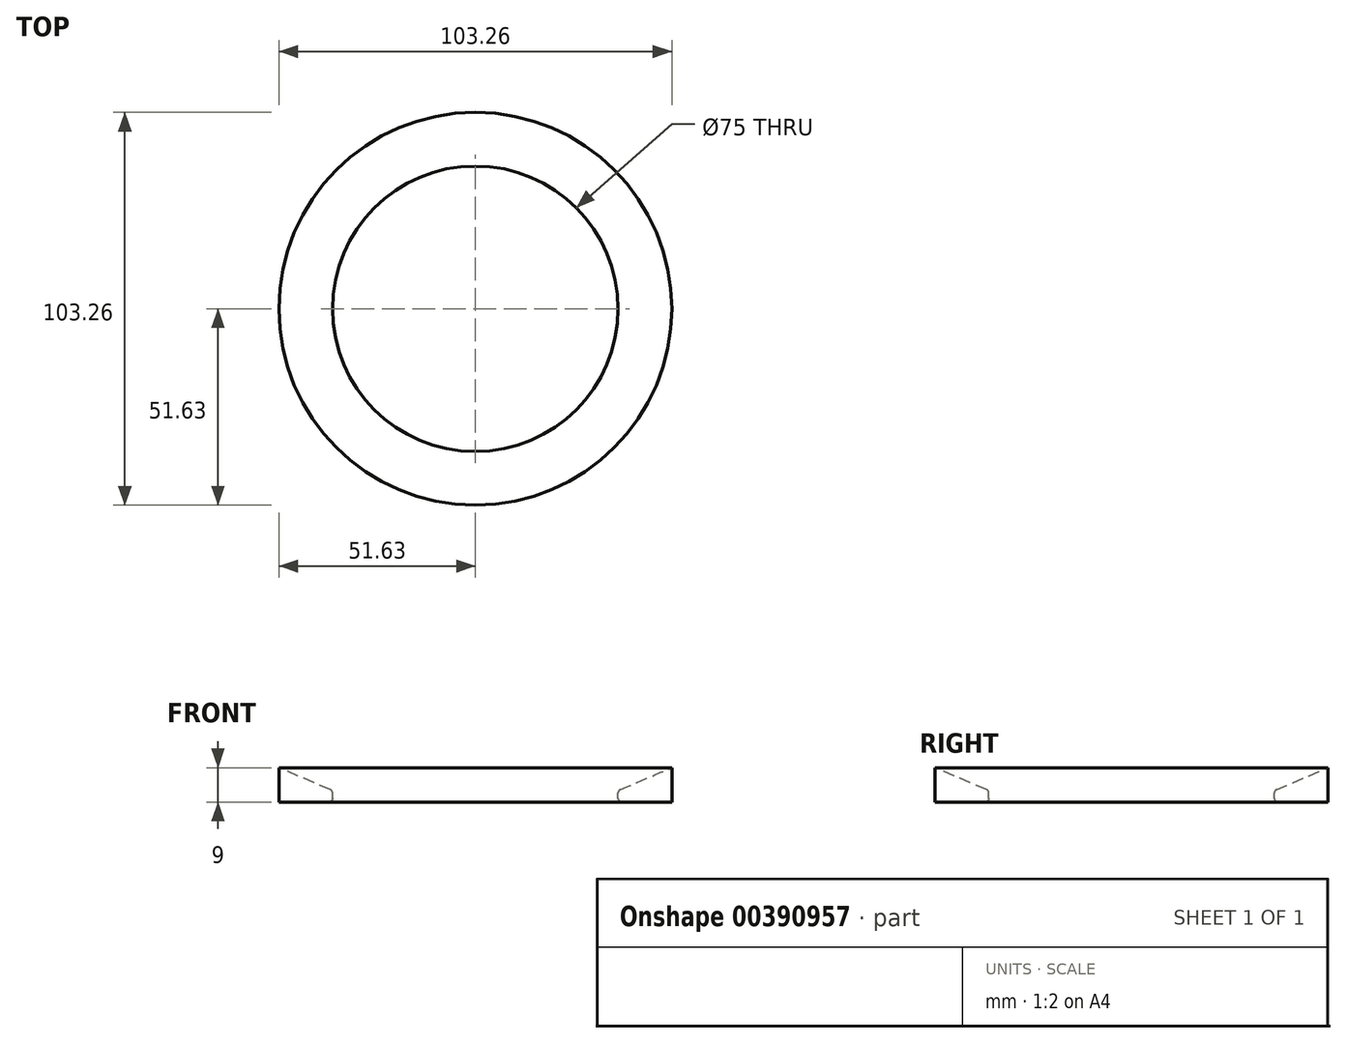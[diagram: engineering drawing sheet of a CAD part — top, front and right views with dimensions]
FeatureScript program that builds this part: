
annotation { "Feature Type Name" : "Feature", "Feature Type Description" : "" }
export const myFeature = defineFeature(function(context is Context, id is Id, definition is map)
    precondition{}
    {
        {
            var Q0;
            Q0=qCreatedBy(makeId("Front.planeOp"),FACE);
            var sketch = newSketch(context, id + "F0", { "sketchPlane" : qUnion([Q0])});
            skLineSegment(sketch, "E0", {"start": v(0, 40.57) * mm, "end": v(0, -40.16) * mm, "construction": true});
            skLineSegment(sketch, "E1", {"start": v(-37.5, -9) * mm, "end": v(-51.63, -9) * mm});
            skLineSegment(sketch, "E2", {"start": v(-51.63, -9) * mm, "end": v(-51.63, 0) * mm});
            skLineSegment(sketch, "E3", {"start": v(-51.63, 0) * mm, "end": v(-37.5, -6) * mm});
            skLineSegment(sketch, "E4", {"start": v(-37.5, -6) * mm, "end": v(-37.5, -9) * mm});
            skLineSegment(sketch, "E5.MirrorCS", {"start": v(37.5, -6) * mm, "end": v(37.5, -9) * mm});
            skLineSegment(sketch, "E6.MirrorCS", {"start": v(51.63, 0) * mm, "end": v(37.5, -6) * mm});
            skLineSegment(sketch, "E7.MirrorCS", {"start": v(51.63, -9) * mm, "end": v(51.63, 0) * mm});
            skLineSegment(sketch, "E8.MirrorCS", {"start": v(37.5, -9) * mm, "end": v(51.63, -9) * mm});
            skSolve(sketch);
        }
        {
            var Q0;
            Q0 = qSketchRegion(id + "F0", true);
            var Q1;
            Q1=sQuery(id+"F0.wireOp",EDGE,"E0");
            revolve(context, id + "F1", {"entities" : qUnion([Q0]), "axis" : qUnion([Q1]), "revolveType" : RevolveType.FULL});
        }
        {
            var Q0;
            Q0=makeQuery(id+"F1.opRevolve","SWEPT_EDGE",EDGE,{"disambiguationData":[OSD([sQuery(id+"F0.wireOp",EDGE,"E1"),sQuery(id+"F0.wireOp",EDGE,"E4")])]});
            fillet(context, id + "F2", {"entities" : qUnion([Q0]), "radius" : 1 * mm, "tangentPropagation" : true, "allowEdgeOverflow" : false});
        }
        {
            var Q0;
            Q0=makeQuery(id+"F1.opRevolve","SWEPT_EDGE",EDGE,{"disambiguationData":[OSD([sQuery(id+"F0.wireOp",EDGE,"E3"),sQuery(id+"F0.wireOp",EDGE,"E4")])]});
            fillet(context, id + "F3", {"entities" : qUnion([Q0]), "radius" : 1 * mm, "tangentPropagation" : true, "allowEdgeOverflow" : false});
        }
        {
            var Q0;
            Q0=makeQuery(id+"F1.opRevolve","SWEPT_BODY",BODY,{"disambiguationData":[OSD([sQuery(id+"F0.wireOp",EDGE,"E5.MirrorCS"),sQuery(id+"F0.wireOp",EDGE,"E6.MirrorCS"),sQuery(id+"F0.wireOp",EDGE,"E7.MirrorCS"),sQuery(id+"F0.wireOp",EDGE,"E8.MirrorCS")])]});
            deleteBodies(context, id + "F4", {"entities" : qUnion([Q0])});
        }
    });
